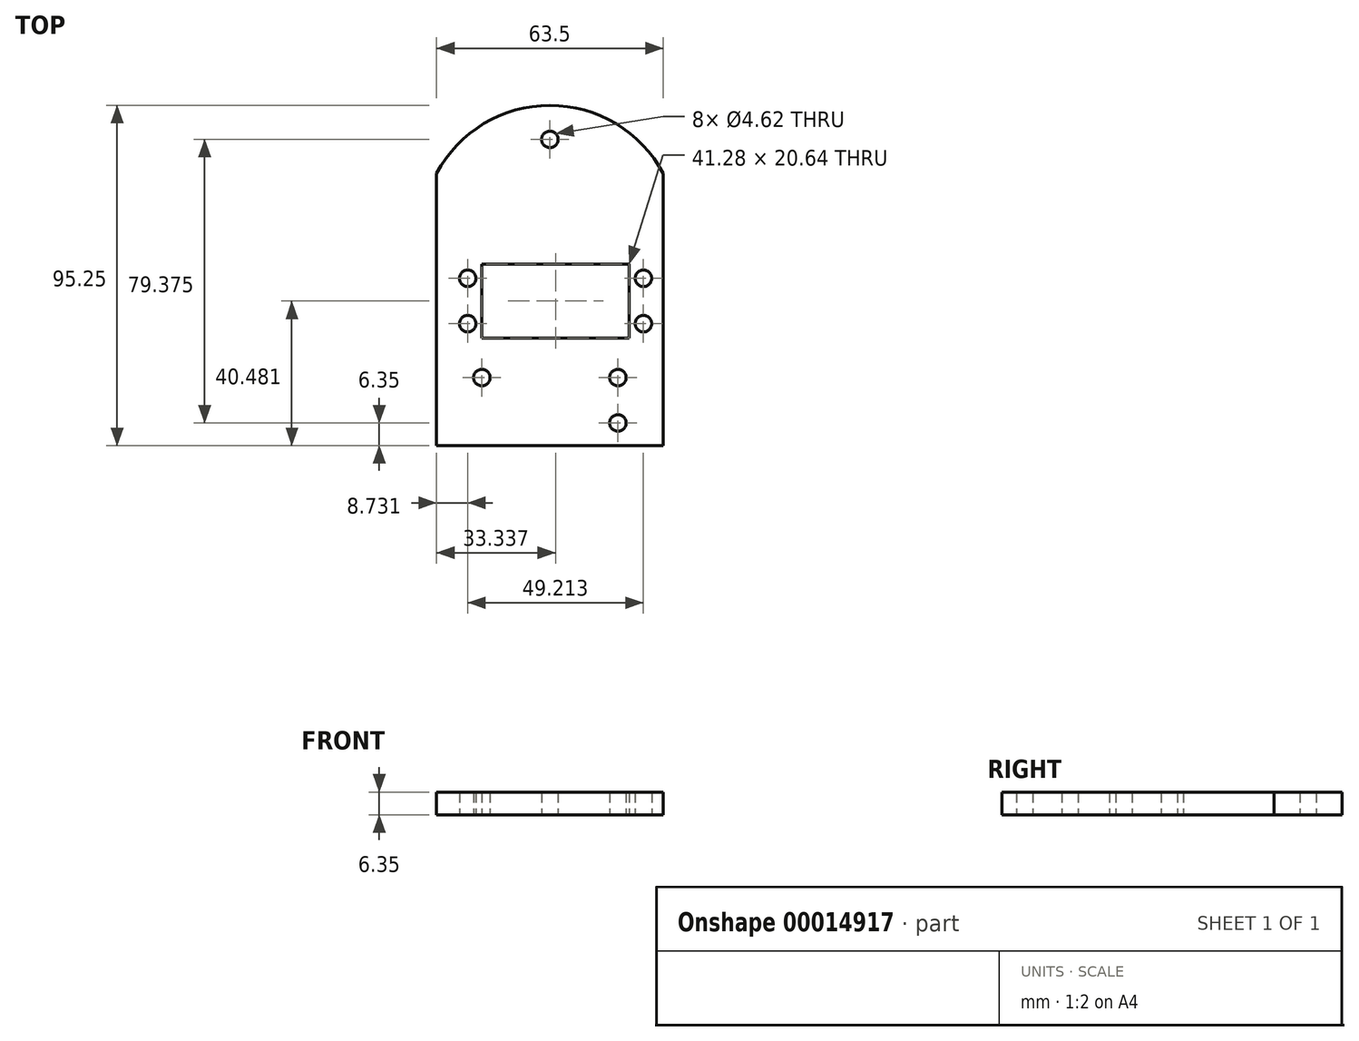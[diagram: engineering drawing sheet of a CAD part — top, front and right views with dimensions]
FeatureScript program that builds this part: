
annotation { "Feature Type Name" : "Feature", "Feature Type Description" : "" }
export const myFeature = defineFeature(function(context is Context, id is Id, definition is map)
    precondition{}
    {
        {
            var Q0;
            Q0=qCreatedBy(makeId("Top.planeOp"),FACE);
            var sketch = newSketch(context, id + "F0", { "sketchPlane" : qUnion([Q0])});
            skLineSegment(sketch, "E0.bottom", {"start": v(0, 76.2) * mm, "end": v(63.5, 76.2) * mm});
            skLineSegment(sketch, "E0.top", {"start": v(0, 0) * mm, "end": v(63.5, 0) * mm});
            skLineSegment(sketch, "E0.left", {"start": v(0, 76.2) * mm, "end": v(0, 0) * mm});
            skLineSegment(sketch, "E0.right", {"start": v(63.5, 76.2) * mm, "end": v(63.5, 0) * mm});
            skCircle(sketch, "E1", {"center": v(50.8, 6.35) * mm, "radius": 2.31 * mm});
            skCircle(sketch, "E2", {"center": v(12.7, 19.05) * mm, "radius": 2.31 * mm});
            skLineSegment(sketch, "E3.bottom", {"start": v(12.7, 50.8) * mm, "end": v(53.98, 50.8) * mm});
            skLineSegment(sketch, "E3.top", {"start": v(12.7, 30.16) * mm, "end": v(53.98, 30.16) * mm});
            skCircle(sketch, "E4", {"center": v(50.8, 19.05) * mm, "radius": 2.31 * mm});
            skLineSegment(sketch, "E3.left", {"start": v(12.7, 50.8) * mm, "end": v(12.7, 30.16) * mm});
            skCircle(sketch, "E5", {"center": v(8.73, 46.83) * mm, "radius": 2.31 * mm});
            skCircle(sketch, "E6", {"center": v(8.73, 34.13) * mm, "radius": 2.31 * mm});
            skCircle(sketch, "E7", {"center": v(57.94, 34.13) * mm, "radius": 2.31 * mm});
            skLineSegment(sketch, "E3.right", {"start": v(53.98, 50.8) * mm, "end": v(53.98, 30.16) * mm});
            skCircle(sketch, "E8", {"center": v(57.94, 46.83) * mm, "radius": 2.31 * mm});
            skCircle(sketch, "E9", {"center": v(31.75, 59.27) * mm, "radius": 35.98 * mm});
            skPoint(sketch, "E9.first.point", {"position": v(33.34, 23.32) * mm});
            skPoint(sketch, "E10", {"position": v(33.34, 30.16) * mm});
            skLineSegment(sketch, "E11", {"start": v(31.75, 76.2) * mm, "end": v(31.75, 95.25) * mm});
            skCircle(sketch, "E12", {"center": v(31.75, 85.72) * mm, "radius": 2.31 * mm});
            skSolve(sketch);
        }
        {
            var Q0;
            {var subQ16=sQuery(id+"F0.wireOp",EDGE,"E0.top");Q0=makeQuery(id+"F0.imprint","IMPRINT",FACE,{"disambiguationData":[TD([[makeQuery(id+"F0.imprint","IMPRINT",EDGE,{"derivedFrom":subQ16}),1.0]])]});}
            var Q1;
            {var subQ16=sQuery(id+"F0.wireOp",EDGE,"E3.bottom");Q1=makeQuery(id+"F0.imprint","IMPRINT",FACE,{"disambiguationData":[TD([[makeQuery(id+"F0.imprint","IMPRINT",EDGE,{"derivedFrom":subQ16}),1.0]])]});}
            var Q2;
            {var subQ0=sQuery(id+"F0.wireOp",EDGE,"E11");Q2=makeQuery(id+"F0.imprint","IMPRINT",FACE,{"disambiguationData":[TD([[makeQuery(id+"F0.imprint","IMPRINT",EDGE,{"derivedFrom":subQ0}),1.0]])]});}
            var Q3;
            {var subQ0=sQuery(id+"F0.wireOp",EDGE,"E11");Q3=makeQuery(id+"F0.imprint","IMPRINT",FACE,{"disambiguationData":[TD([[makeQuery(id+"F0.imprint","IMPRINT",EDGE,{"derivedFrom":subQ0}),-1.0]])]});}
            extrude(context, id + "F1", {"entities" : qUnion([Q0, Q1, Q2, Q3]), "depth" : 6.35 * mm});
        }
    });
